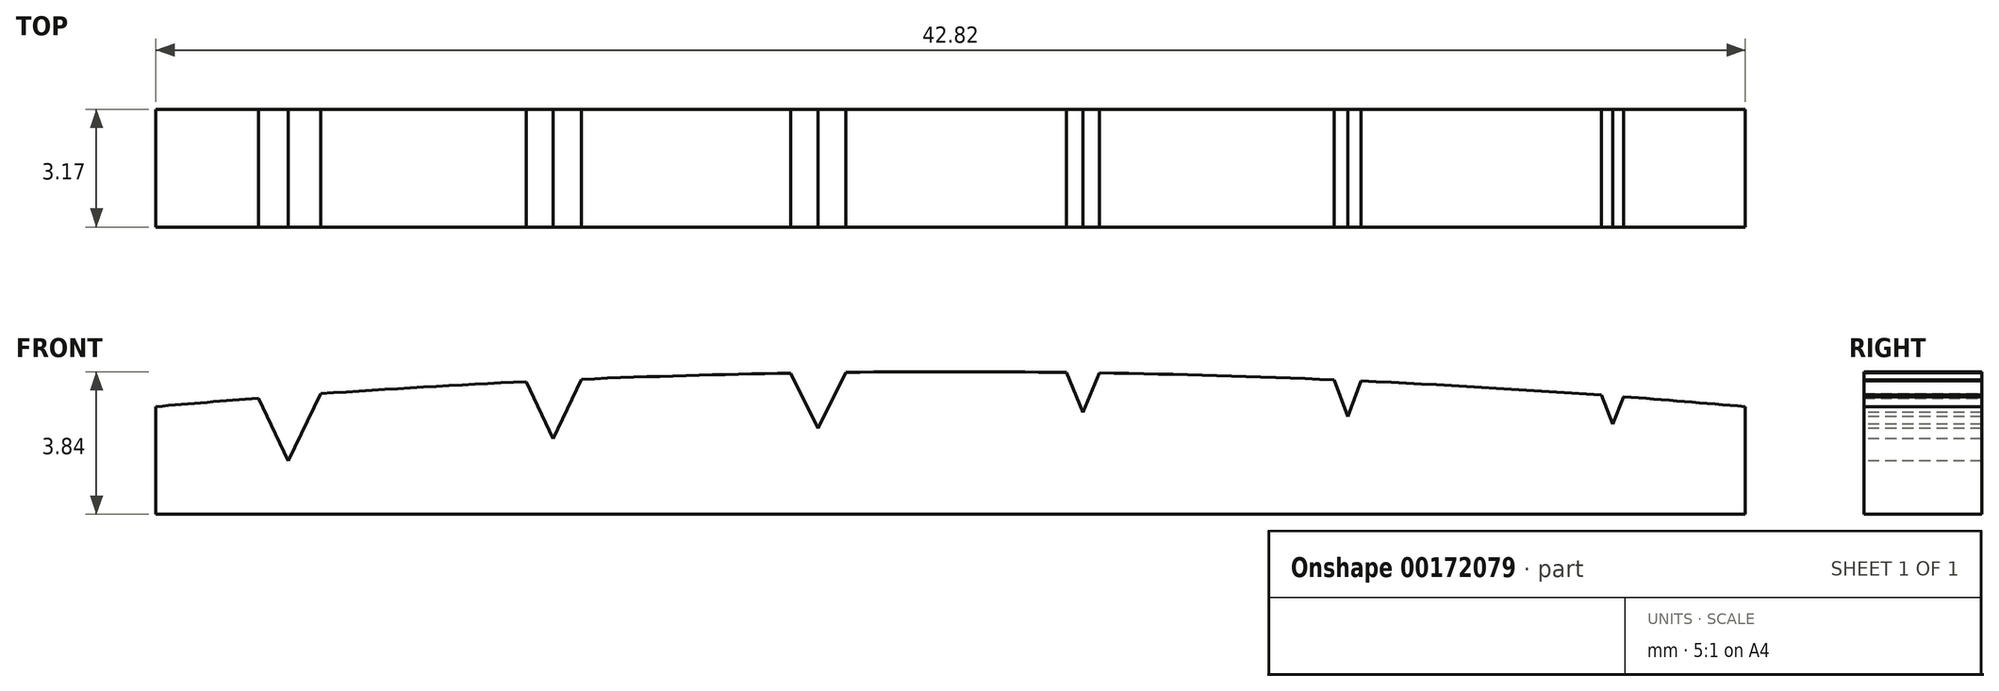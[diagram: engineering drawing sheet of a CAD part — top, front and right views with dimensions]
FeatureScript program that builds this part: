
annotation { "Feature Type Name" : "Feature", "Feature Type Description" : "" }
export const myFeature = defineFeature(function(context is Context, id is Id, definition is map)
    precondition{}
    {
        {
            var Q0;
            Q0=qCreatedBy(makeId("Top.planeOp"),FACE);
            var sketch = newSketch(context, id + "F0", { "sketchPlane" : qUnion([Q0])});
            skLineSegment(sketch, "E0.bottom", {"start": v(-21.41, 1.59) * mm, "end": v(21.41, 1.59) * mm});
            skLineSegment(sketch, "E0.top", {"start": v(-21.41, -1.59) * mm, "end": v(21.41, -1.59) * mm});
            skLineSegment(sketch, "E0.left", {"start": v(-21.41, 1.59) * mm, "end": v(-21.41, -1.59) * mm});
            skLineSegment(sketch, "E0.right", {"start": v(21.41, 1.59) * mm, "end": v(21.41, -1.59) * mm});
            skPoint(sketch, "E0.middle", {"position": v(0, 0) * mm});
            skLineSegment(sketch, "E1", {"start": v(-3.57, 1.59) * mm, "end": v(-3.57, -56.89) * mm, "construction": true});
            skLineSegment(sketch, "E2", {"start": v(3.57, 1.59) * mm, "end": v(3.57, -28.96) * mm, "construction": true});
            skLineSegment(sketch, "E3", {"start": v(0, 0) * mm, "end": v(0, -5.88) * mm, "construction": true});
            skPoint(sketch, "E3.endSnap0", {"position": v(0, -1.59) * mm});
            skLineSegment(sketch, "E4.1.0.0", {"start": v(10.7, 1.59) * mm, "end": v(10.7, -28.96) * mm, "construction": true});
            skLineSegment(sketch, "E4.2.0.0", {"start": v(17.84, 1.59) * mm, "end": v(17.84, -28.96) * mm, "construction": true});
            skLineSegment(sketch, "E4.direction1", {"start": v(3.57, -28.96) * mm, "end": v(10.7, -28.96) * mm, "construction": true});
            skLineSegment(sketch, "E5.1.0.0", {"start": v(-10.7, 1.59) * mm, "end": v(-10.7, -56.89) * mm, "construction": true});
            skLineSegment(sketch, "E5.2.0.0", {"start": v(-17.84, 1.59) * mm, "end": v(-17.84, -56.89) * mm, "construction": true});
            skLineSegment(sketch, "E5.direction1", {"start": v(-3.57, -56.89) * mm, "end": v(-10.7, -56.89) * mm, "construction": true});
            skSolve(sketch);
        }
        {
            var Q0;
            Q0=qCreatedBy(makeId("Front.planeOp"),FACE);
            var sketch = newSketch(context, id + "F1", { "sketchPlane" : qUnion([Q0])});
            skArc(sketch, "E6", {"start": v(21.41, -0.94) * mm, "mid": v(0, 0) * mm, "end": v(-21.41, -0.94) * mm});
            skLineSegment(sketch, "E7", {"start": v(21.41, -0.94) * mm, "end": v(21.41, -3.84) * mm});
            skLineSegment(sketch, "E8", {"start": v(-21.41, -0.94) * mm, "end": v(-21.41, -3.84) * mm});
            skArc(sketch, "E9", {"start": v(21.41, -3.84) * mm, "mid": v(0, -2.89) * mm, "end": v(-21.41, -3.84) * mm});
            skLineSegment(sketch, "E10", {"start": v(-21.41, -3.84) * mm, "end": v(21.41, -3.84) * mm});
            skSolve(sketch);
        }
        {
            var Q0;
            Q0 = qSketchRegion(id + "F1", true);
            extrude(context, id + "F2", {"entities" : qUnion([Q0]), "depth" : 3.17 * mm});
        }
        {
            var Q0;
            Q0=makeQuery(id+"F2.opExtrude","CAP_FACE",FACE,{"disambiguationData":[OSD([sQuery(id+"F1.wireOp",EDGE,"E6"),sQuery(id+"F1.wireOp",EDGE,"E7"),sQuery(id+"F1.wireOp",EDGE,"E8"),sQuery(id+"F1.wireOp",EDGE,"E9")])],"isStart":false});
            var sketch = newSketch(context, id + "F3", { "sketchPlane" : qUnion([Q0])});
            skPoint(sketch, "E11.center", {"position": v(0, -243.83) * mm});
            skLineSegment(sketch, "E12", {"start": v(-19, 0) * mm, "end": v(-17.84, -2.4) * mm});
            skLineSegment(sketch, "E13", {"start": v(-17.84, -2.4) * mm, "end": v(-16.7, 0) * mm});
            skLineSegment(sketch, "E14", {"start": v(-16.7, 0) * mm, "end": v(-19, 0) * mm});
            skLineSegment(sketch, "E15.1.0.0", {"start": v(-11.56, 0) * mm, "end": v(-10.7, -1.8) * mm});
            skLineSegment(sketch, "E15.1.0.1", {"start": v(-10.7, -1.8) * mm, "end": v(-9.85, 0) * mm});
            skLineSegment(sketch, "E15.1.0.2", {"start": v(-9.85, 0) * mm, "end": v(-11.56, 0) * mm});
            skLineSegment(sketch, "E15.2.0.0", {"start": v(-4.33, 0) * mm, "end": v(-3.57, -1.53) * mm});
            skLineSegment(sketch, "E15.2.0.1", {"start": v(-3.57, -1.53) * mm, "end": v(-2.81, 0) * mm});
            skLineSegment(sketch, "E15.2.0.2", {"start": v(-2.81, 0) * mm, "end": v(-4.33, 0) * mm});
            skLineSegment(sketch, "E16.0.3.0", {"start": v(3.1, 0) * mm, "end": v(3.57, -1.1) * mm});
            skLineSegment(sketch, "E16.3.3.0", {"start": v(3.57, -1.1) * mm, "end": v(4.03, 0) * mm});
            skLineSegment(sketch, "E16.6.3.0", {"start": v(4.03, 0) * mm, "end": v(3.1, 0) * mm});
            skLineSegment(sketch, "E16.0.4.0", {"start": v(10.25, 0) * mm, "end": v(10.7, -1.22) * mm});
            skLineSegment(sketch, "E16.3.4.0", {"start": v(10.7, -1.22) * mm, "end": v(11.16, 0) * mm});
            skLineSegment(sketch, "E16.6.4.0", {"start": v(11.16, 0) * mm, "end": v(10.25, 0) * mm});
            skLineSegment(sketch, "E16.0.5.0", {"start": v(17.44, -0.38) * mm, "end": v(17.84, -1.42) * mm});
            skLineSegment(sketch, "E16.3.5.0", {"start": v(17.84, -1.42) * mm, "end": v(18.24, -0.38) * mm});
            skLineSegment(sketch, "E16.6.5.0", {"start": v(18.24, -0.38) * mm, "end": v(17.44, -0.38) * mm});
            skSolve(sketch);
        }
        {
            var Q0;
            Q0 = qSketchRegion(id + "F3", true);
            extrude(context, id + "F4", {"entities" : qUnion([Q0]), "operationType" : NewBodyOperationType.REMOVE, "endBound" : BoundingType.THROUGH_ALL, "oppositeDirection" : true, "depth" : 25.4 * mm});
        }
    });
